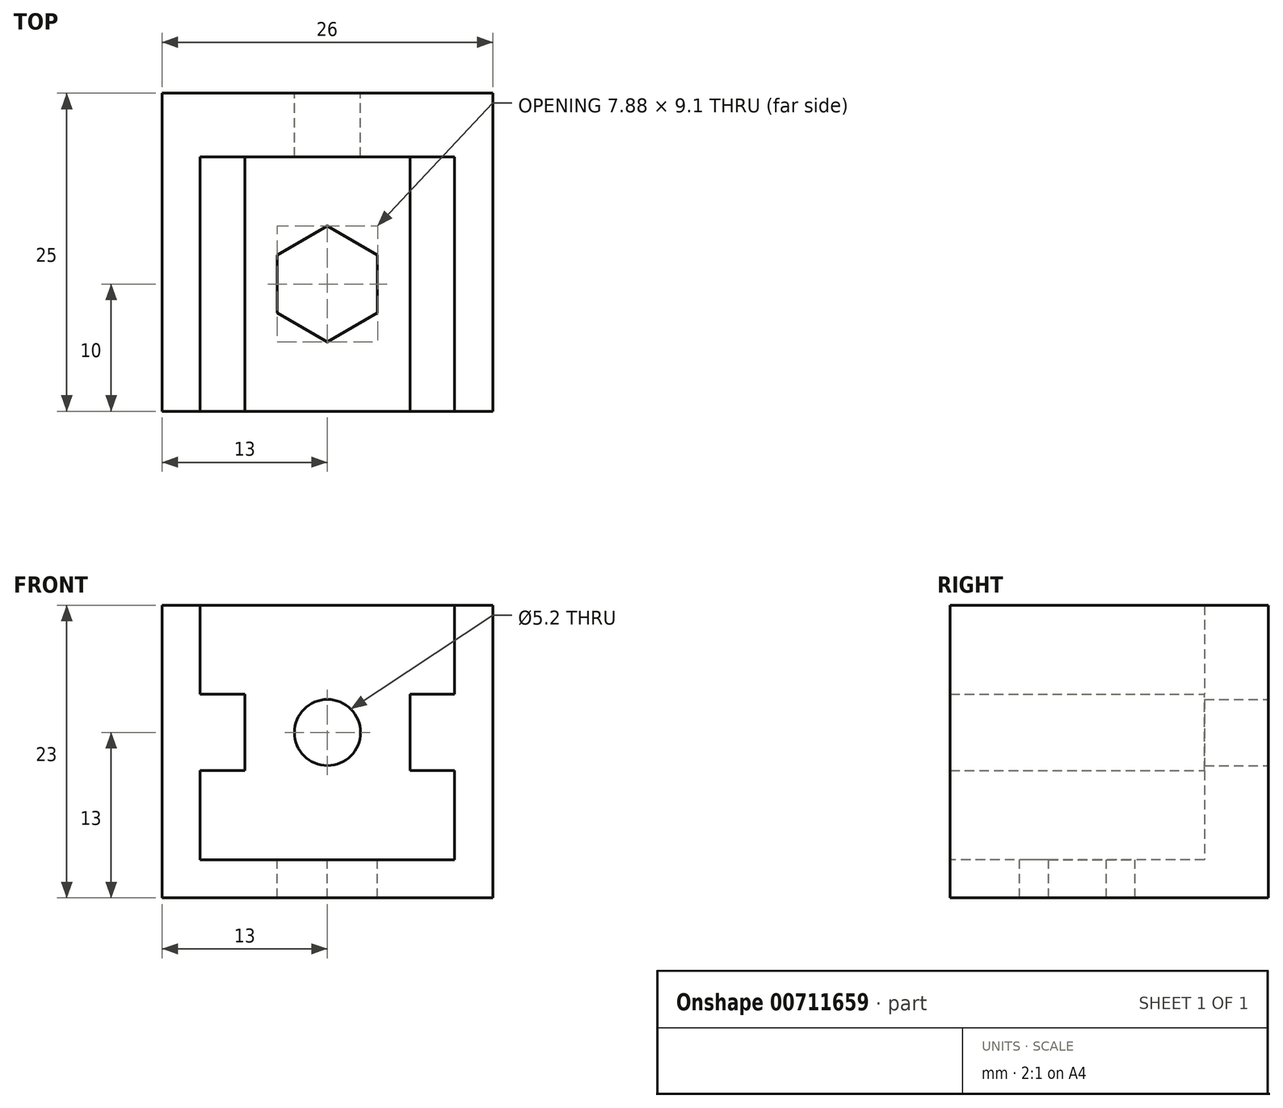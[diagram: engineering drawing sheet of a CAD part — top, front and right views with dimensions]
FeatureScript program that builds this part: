
annotation { "Feature Type Name" : "Feature", "Feature Type Description" : "" }
export const myFeature = defineFeature(function(context is Context, id is Id, definition is map)
    precondition{}
    {
        {
            var Q0;
            Q0=qCreatedBy(makeId("Top.planeOp"),FACE);
            var sketch = newSketch(context, id + "F0", { "sketchPlane" : qUnion([Q0])});
            skLineSegment(sketch, "E0.bottom", {"start": v(-10, 10) * mm, "end": v(10, 10) * mm});
            skLineSegment(sketch, "E0.top", {"start": v(-10, -10) * mm, "end": v(10, -10) * mm});
            skLineSegment(sketch, "E0.right", {"start": v(10, 10) * mm, "end": v(10, -10) * mm});
            skPoint(sketch, "E0.middle", {"position": v(0, 0) * mm});
            skCircle(sketch, "E1", {"center": v(0, 0) * mm, "radius": 2.1 * mm, "construction": true});
            skLineSegment(sketch, "E2.bottom", {"start": v(-13, 15) * mm, "end": v(13, 15) * mm});
            skLineSegment(sketch, "E3.bottom", {"start": v(10, -10) * mm, "end": v(13, -10) * mm});
            skLineSegment(sketch, "E3.right", {"start": v(13, -10) * mm, "end": v(13, 15) * mm});
            skLineSegment(sketch, "E4.bottom", {"start": v(-10, -10) * mm, "end": v(-13, -10) * mm});
            skLineSegment(sketch, "E4.right", {"start": v(-13, -10) * mm, "end": v(-13, 15) * mm});
            skLineSegment(sketch, "E5", {"start": v(-10, 10) * mm, "end": v(-10, -10) * mm});
            skCircle(sketch, "E6.cCircle", {"center": v(0, 0) * mm, "radius": 3.94 * mm, "construction": true});
            skLineSegment(sketch, "E6.0", {"start": v(0, -4.55) * mm, "end": v(-3.94, -2.27) * mm});
            skLineSegment(sketch, "E6.1", {"start": v(-3.94, -2.27) * mm, "end": v(-3.94, 2.27) * mm});
            skLineSegment(sketch, "E6.2", {"start": v(-3.94, 2.27) * mm, "end": v(0, 4.55) * mm});
            skLineSegment(sketch, "E6.3", {"start": v(0, 4.55) * mm, "end": v(3.94, 2.27) * mm});
            skLineSegment(sketch, "E6.4", {"start": v(3.94, 2.27) * mm, "end": v(3.94, -2.27) * mm});
            skLineSegment(sketch, "E6.5", {"start": v(3.94, -2.27) * mm, "end": v(0, -4.55) * mm});
            skPoint(sketch, "E6.0.midPoint", {"position": v(-1.97, -3.41) * mm});
            skSolve(sketch);
        }
        {
            var Q0;
            Q0=makeQuery(id+"F0.imprint","IMPRINT",FACE,{"disambiguationData":[TD([[makeQuery(id+"F0.imprint","IMPRINT",EDGE,{"derivedFrom":sQuery(id+"F0.wireOp",EDGE,"E0.bottom")}),1.0]])]});
            extrude(context, id + "F1", {"entities" : qUnion([Q0]), "depth" : 20 * mm, "offsetDistance" : 25 * mm});
        }
        {
            var Q0;
            Q0=makeQuery(id+"F0.imprint","IMPRINT",FACE,{"disambiguationData":[TD([[makeQuery(id+"F0.imprint","IMPRINT",EDGE,{"derivedFrom":sQuery(id+"F0.wireOp",EDGE,"E0.bottom")}),1.0]])]});
            var Q1;
            Q1=makeQuery(id+"F0.imprint","IMPRINT",FACE,{"disambiguationData":[TD([[makeQuery(id+"F0.imprint","IMPRINT",EDGE,{"derivedFrom":sQuery(id+"F0.wireOp",EDGE,"E0.bottom")}),-1.0]])]});
            extrude(context, id + "F2", {"entities" : qUnion([Q0, Q1]), "operationType" : NewBodyOperationType.ADD, "oppositeDirection" : true, "depth" : 3 * mm, "offsetDistance" : 25 * mm});
        }
        {
            var Q0;
            {var subQ0=sQuery(id+"F0.wireOp",EDGE,"E2.bottom");Q0=makeQuery(id+"F2.boolean.opBoolean","MERGE",FACE,{"derivedFrom":[makeQuery(id+"F1.opExtrude","SWEPT_FACE",FACE,{"disambiguationData":[OSD([subQ0])]}),makeQuery(id+"F2.opExtrude","SWEPT_FACE",FACE,{"disambiguationData":[OSD([subQ0])]})]});}
            var sketch = newSketch(context, id + "F3", { "sketchPlane" : qUnion([Q0])});
            skPoint(sketch, "E7.0", {"position": v(10, 20) * mm});
            skPoint(sketch, "E7.1", {"position": v(-10, 20) * mm});
            skPoint(sketch, "E8.0", {"position": v(-10, 0) * mm});
            skPoint(sketch, "E8.1", {"position": v(10, 0) * mm});
            skLineSegment(sketch, "E9.bottom", {"start": v(10, 0) * mm, "end": v(-10, 0) * mm, "construction": true});
            skLineSegment(sketch, "E9.top", {"start": v(10, 20) * mm, "end": v(-10, 20) * mm, "construction": true});
            skLineSegment(sketch, "E9.left", {"start": v(10, 0) * mm, "end": v(10, 20) * mm, "construction": true});
            skLineSegment(sketch, "E9.right", {"start": v(-10, 0) * mm, "end": v(-10, 20) * mm, "construction": true});
            skCircle(sketch, "E10", {"center": v(0, 10) * mm, "radius": 2.6 * mm});
            skPoint(sketch, "E10.centerSnap0", {"position": v(10, 10) * mm});
            skPoint(sketch, "E10.centerSnap1", {"position": v(0, 20) * mm});
            skLineSegment(sketch, "E11.bottom", {"start": v(10, 7) * mm, "end": v(6.5, 7) * mm});
            skLineSegment(sketch, "E11.top", {"start": v(10, 13) * mm, "end": v(6.5, 13) * mm});
            skLineSegment(sketch, "E11.left", {"start": v(10, 7) * mm, "end": v(10, 13) * mm});
            skLineSegment(sketch, "E11.right", {"start": v(6.5, 7) * mm, "end": v(6.5, 13) * mm});
            skLineSegment(sketch, "E12.bottom", {"start": v(-10, 13) * mm, "end": v(-6.5, 13) * mm});
            skLineSegment(sketch, "E12.top", {"start": v(-10, 7) * mm, "end": v(-6.5, 7) * mm});
            skLineSegment(sketch, "E12.left", {"start": v(-10, 13) * mm, "end": v(-10, 7) * mm});
            skLineSegment(sketch, "E12.right", {"start": v(-6.5, 13) * mm, "end": v(-6.5, 7) * mm});
            skPoint(sketch, "E13", {"position": v(6.5, 10) * mm});
            skSolve(sketch);
        }
        {
            var Q0;
            Q0=makeQuery(id+"F3.imprint","IMPRINT",FACE,{"disambiguationData":[TD([[makeQuery(id+"F3.imprint","IMPRINT",EDGE,{"derivedFrom":sQuery(id+"F3.wireOp",EDGE,"E10")}),1.0]])]});
            extrude(context, id + "F4", {"entities" : qUnion([Q0]), "operationType" : NewBodyOperationType.REMOVE, "endBound" : BoundingType.THROUGH_ALL, "oppositeDirection" : true, "depth" : 25 * mm, "offsetDistance" : 25 * mm});
        }
        {
            var Q0;
            Q0=makeQuery(id+"F3.imprint","IMPRINT",FACE,{"disambiguationData":[TD([[makeQuery(id+"F3.imprint","IMPRINT",EDGE,{"derivedFrom":sQuery(id+"F3.wireOp",EDGE,"E12.bottom")}),-1.0]])]});
            var Q1;
            Q1=makeQuery(id+"F3.imprint","IMPRINT",FACE,{"disambiguationData":[TD([[makeQuery(id+"F3.imprint","IMPRINT",EDGE,{"derivedFrom":sQuery(id+"F3.wireOp",EDGE,"E11.bottom")}),-1.0]])]});
            var Q2;
            {var subQ0=sQuery(id+"F0.wireOp",EDGE,"E4.bottom");var subQ1=sQuery(id+"F0.wireOp",EDGE,"E3.bottom");Q2=makeQuery(id+"F2.boolean.opBoolean","MERGE",FACE,{"derivedFrom":[makeQuery(id+"F1.opExtrude","SWEPT_FACE",FACE,{"disambiguationData":[OSD([subQ1])]}),makeQuery(id+"F1.opExtrude","SWEPT_FACE",FACE,{"disambiguationData":[OSD([subQ0])]}),makeQuery(id+"F2.opExtrude","SWEPT_FACE",FACE,{"disambiguationData":[OSD([sQuery(id+"F0.wireOp",EDGE,"E0.top"),subQ1,subQ0])]})]});}
            extrude(context, id + "F5", {"entities" : qUnion([Q0, Q1]), "operationType" : NewBodyOperationType.ADD, "endBound" : BoundingType.UP_TO_SURFACE, "oppositeDirection" : true, "depth" : 25 * mm, "endBoundEntityFace" : qUnion([Q2]), "offsetDistance" : 25 * mm});
        }
    });
